# Revit family: Zurn_One-System-Zurn-ZWC1S
name_source: partatom
category: Plumbing Fixtures
units: mm (PartAtom-declared; Revit-internal decimal feet)

## family parameters
Always vertical = Yes
Cut with Voids When Loaded = No
Maintain Annotation Orientation = No
OmniClass Number = 23.45.05.00
OmniClass Title = Sanitary Equipment
Part Type = Normal
Room Calculation Point = No
Round Connector Dimension = Use Radius
Shared = No
Work Plane-Based = No

## types (1)
- Z.WC1.S (Zurn One Sensor Wall Hung Toilet System)
    Activation method = Sensor
    Assembly Code = D2010
    CW Connection = Yes
    CWFU = 1
    Default Elevation = 0 "
    Description = Zurn One Sensor Wall Hung Toilet System with 1.1 GPF EcoVantage® Battery Powered Flush Valve
    Distance between Flush Valve Hole to the Back of the Bowl = 2.75 "
    Fixture Material = Vitreous China - Zurn - White
    Fixture Number = Z5615-BWL
    Flush Rate (GPF) = 1.1 GPF
    Flush Valve Number = ZER6000AV-ONE-SM
    HW Connection = No
    HWFU = 0
    Height of Bowl = 13.25 "
    Inlet Connection Size (inch) = 1 "
    Manufacturer = Zurn
    Manufacturer Brand = Zurn Water, LLC
    Max Working Water Temperature = 104 °F
    Mode of Installation = Wall Mounted
    Model = Z.WC1.S
    Modified Date = 02/03/2026
    Operating Water Pressure (PSI) = 25 – 80 PSI (172 – 552 kPa)
    Outlet Connection Size (inch) = 1 "
    Product Documentation Link = https://files.zurn.com
    Product Page URL = https://www.zurn.com
    Product data URL = https://bimobject.com
    Seat Number = Z5955SS-EL
    URL = https://www.zurn.com
    Vent Connection = No
    WFU = 1
    Waste Connection = Yes

## geometry (parser evidence)
native form markers: Blend x10, Sweep x25
no freeform markers — native parametric forms only
